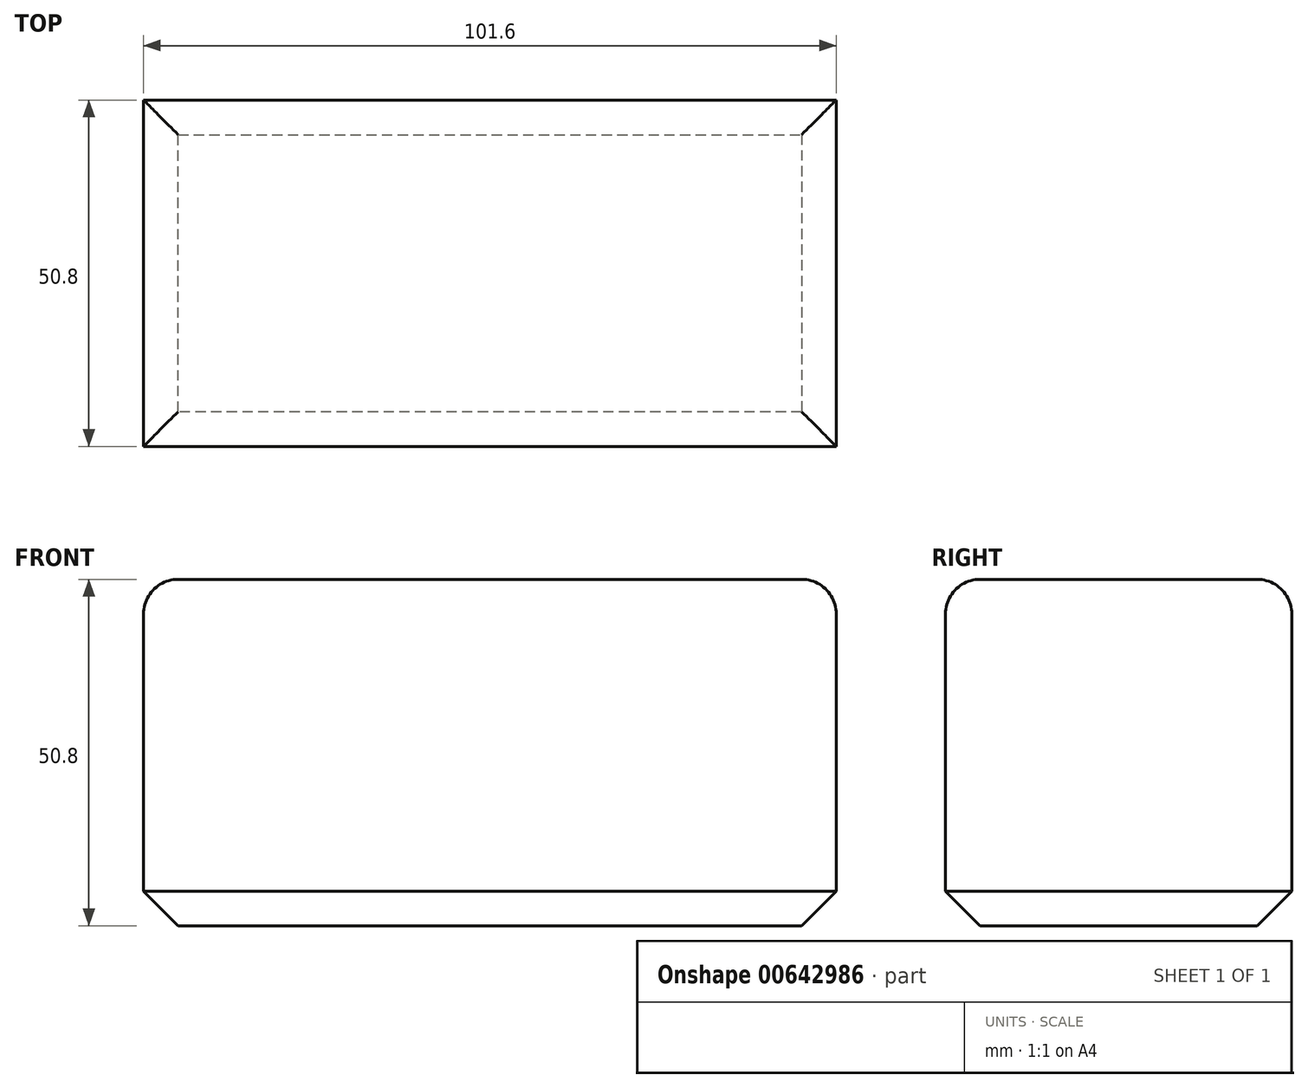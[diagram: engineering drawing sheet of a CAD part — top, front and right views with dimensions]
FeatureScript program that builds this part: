
annotation { "Feature Type Name" : "Feature", "Feature Type Description" : "" }
export const myFeature = defineFeature(function(context is Context, id is Id, definition is map)
    precondition{}
    {
        {
            var Q0;
            Q0=qCreatedBy(makeId("Top.planeOp"),FACE);
            var sketch = newSketch(context, id + "F0", { "sketchPlane" : qUnion([Q0])});
            skLineSegment(sketch, "E0.bottom", {"start": v(-14.87, 30.36) * mm, "end": v(86.73, 30.36) * mm});
            skLineSegment(sketch, "E0.top", {"start": v(-14.87, -20.44) * mm, "end": v(86.73, -20.44) * mm});
            skLineSegment(sketch, "E0.left", {"start": v(-14.87, 30.36) * mm, "end": v(-14.87, -20.44) * mm});
            skLineSegment(sketch, "E0.right", {"start": v(86.73, 30.36) * mm, "end": v(86.73, -20.44) * mm});
            skSolve(sketch);
        }
        {
            var Q0;
            Q0 = qSketchRegion(id + "F0", true);
            extrude(context, id + "F1", {"entities" : qUnion([Q0]), "depth" : 50.8 * mm, "offsetDistance" : 25.4 * mm});
        }
        {
            var Q0;
            Q0=makeQuery(id+"F1.opExtrude","CAP_FACE",FACE,{"disambiguationData":[OSD([sQuery(id+"F0.wireOp",EDGE,"E0.bottom"),sQuery(id+"F0.wireOp",EDGE,"E0.top"),sQuery(id+"F0.wireOp",EDGE,"E0.left"),sQuery(id+"F0.wireOp",EDGE,"E0.right")])],"isStart":false});
            fillet(context, id + "F2", {"entities" : qUnion([Q0]), "radius" : 5.08 * mm, "tangentPropagation" : true, "allowEdgeOverflow" : false});
        }
        {
            var Q0;
            Q0=makeQuery(id+"F1.opExtrude","CAP_FACE",FACE,{"disambiguationData":[OSD([sQuery(id+"F0.wireOp",EDGE,"E0.bottom"),sQuery(id+"F0.wireOp",EDGE,"E0.top"),sQuery(id+"F0.wireOp",EDGE,"E0.left"),sQuery(id+"F0.wireOp",EDGE,"E0.right")])],"isStart":true});
            chamfer(context, id + "F3", {"entities" : qUnion([Q0]), "width" : 5.08 * mm, "tangentPropagation" : true});
        }
    });
